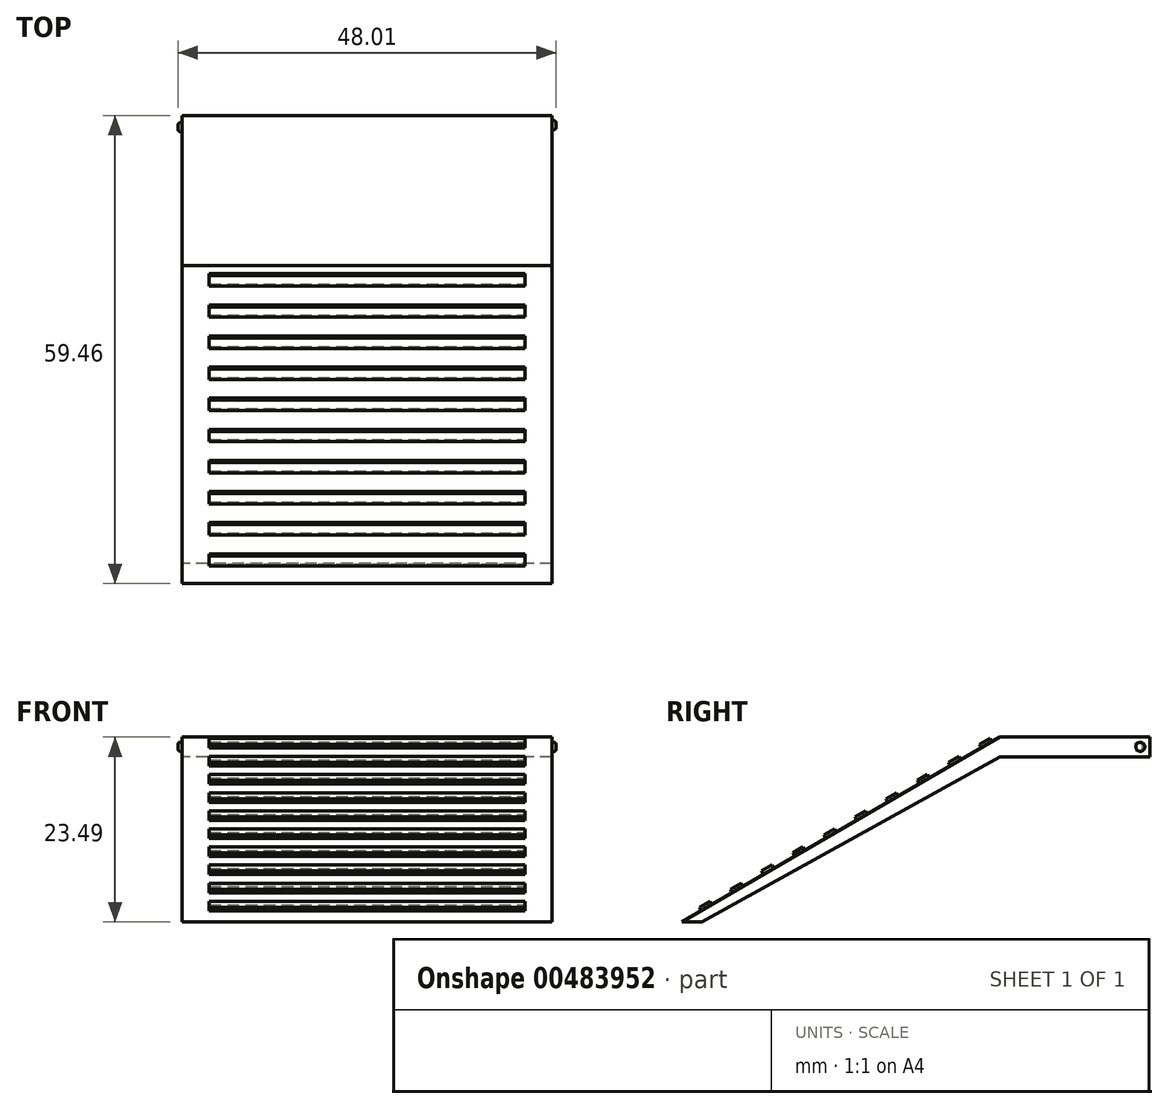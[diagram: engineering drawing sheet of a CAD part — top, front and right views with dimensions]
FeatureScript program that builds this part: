
annotation { "Feature Type Name" : "Feature", "Feature Type Description" : "" }
export const myFeature = defineFeature(function(context is Context, id is Id, definition is map)
    precondition{}
    {
        {
            var Q0;
            Q0=qCreatedBy(makeId("Right.planeOp"),FACE);
            var sketch = newSketch(context, id + "F0", { "sketchPlane" : qUnion([Q0])});
            skLineSegment(sketch, "E0.bottom", {"start": v(19.05, 2.54) * mm, "end": v(0, 2.54) * mm});
            skLineSegment(sketch, "E0.top", {"start": v(19.05, 0) * mm, "end": v(0, 0) * mm});
            skLineSegment(sketch, "E0.left", {"start": v(19.05, 2.54) * mm, "end": v(19.05, 0) * mm});
            skLineSegment(sketch, "E0.right", {"start": v(0, 2.54) * mm, "end": v(0, 0) * mm});
            skLineSegment(sketch, "E1", {"start": v(0, 2.54) * mm, "end": v(-40.41, -20.95) * mm});
            skLineSegment(sketch, "E2", {"start": v(-40.41, -20.95) * mm, "end": v(-37.87, -20.95) * mm});
            skLineSegment(sketch, "E3", {"start": v(-37.87, -20.95) * mm, "end": v(0, 0) * mm});
            skSolve(sketch);
        }
        {
            var Q0;
            Q0=makeQuery(id+"F0.imprint","IMPRINT",FACE,{"disambiguationData":[TD([[makeQuery(id+"F0.imprint","IMPRINT",EDGE,{"derivedFrom":sQuery(id+"F0.wireOp",EDGE,"E0.bottom")}),1.0]])]});
            var Q1;
            Q1=makeQuery(id+"F0.imprint","IMPRINT",FACE,{"disambiguationData":[TD([[makeQuery(id+"F0.imprint","IMPRINT",EDGE,{"derivedFrom":sQuery(id+"F0.wireOp",EDGE,"E0.right")}),-1.0]])]});
            extrude(context, id + "F1", {"entities" : qUnion([Q0, Q1]), "depth" : 47 * mm});
        }
        {
            var Q0;
            Q0=makeQuery(id+"F1.opExtrude","SWEPT_FACE",FACE,{"disambiguationData":[OSD([sQuery(id+"F0.wireOp",EDGE,"E1")])]});
            var sketch = newSketch(context, id + "F2", { "sketchPlane" : qUnion([Q0])});
            skLineSegment(sketch, "E4.bottom", {"start": v(3.45, -1.47) * mm, "end": v(43.54, -1.47) * mm});
            skLineSegment(sketch, "E4.top", {"start": v(3.45, 0.06) * mm, "end": v(43.54, 0.06) * mm});
            skLineSegment(sketch, "E4.left", {"start": v(3.45, -1.47) * mm, "end": v(3.45, 0.06) * mm});
            skLineSegment(sketch, "E4.right", {"start": v(43.54, -1.47) * mm, "end": v(43.54, 0.06) * mm});
            skPoint(sketch, "E4.middle", {"position": v(23.5, -0.7) * mm});
            skPoint(sketch, "E4.middle.positionSnap0", {"position": v(23.5, 1.28) * mm});
            skPoint(sketch, "E4.centerSnap0", {"position": v(23.5, 1.28) * mm});
            skLineSegment(sketch, "E5.0.1.0", {"start": v(3.45, -6.04) * mm, "end": v(3.45, -4.52) * mm});
            skLineSegment(sketch, "E5.0.1.1", {"start": v(3.45, -4.52) * mm, "end": v(43.54, -4.52) * mm});
            skLineSegment(sketch, "E5.0.1.2", {"start": v(43.54, -6.04) * mm, "end": v(43.54, -4.52) * mm});
            skLineSegment(sketch, "E5.0.1.3", {"start": v(3.45, -6.04) * mm, "end": v(43.54, -6.04) * mm});
            skLineSegment(sketch, "E5.0.2.0", {"start": v(3.45, -10.61) * mm, "end": v(3.45, -9.09) * mm});
            skLineSegment(sketch, "E5.0.2.1", {"start": v(3.45, -9.09) * mm, "end": v(43.54, -9.09) * mm});
            skLineSegment(sketch, "E5.0.2.2", {"start": v(43.54, -10.61) * mm, "end": v(43.54, -9.09) * mm});
            skLineSegment(sketch, "E5.0.2.3", {"start": v(3.45, -10.61) * mm, "end": v(43.54, -10.61) * mm});
            skLineSegment(sketch, "E5.0.3.0", {"start": v(3.45, -15.18) * mm, "end": v(3.45, -13.66) * mm});
            skLineSegment(sketch, "E5.0.3.1", {"start": v(3.45, -13.66) * mm, "end": v(43.54, -13.66) * mm});
            skLineSegment(sketch, "E5.0.3.2", {"start": v(43.54, -15.18) * mm, "end": v(43.54, -13.66) * mm});
            skLineSegment(sketch, "E5.0.3.3", {"start": v(3.45, -15.18) * mm, "end": v(43.54, -15.18) * mm});
            skLineSegment(sketch, "E5.0.4.0", {"start": v(3.45, -19.76) * mm, "end": v(3.45, -18.23) * mm});
            skLineSegment(sketch, "E5.0.4.1", {"start": v(3.45, -18.23) * mm, "end": v(43.54, -18.23) * mm});
            skLineSegment(sketch, "E5.0.4.2", {"start": v(43.54, -19.76) * mm, "end": v(43.54, -18.23) * mm});
            skLineSegment(sketch, "E5.0.4.3", {"start": v(3.45, -19.76) * mm, "end": v(43.54, -19.76) * mm});
            skLineSegment(sketch, "E5.0.5.0", {"start": v(3.45, -24.33) * mm, "end": v(3.45, -22.8) * mm});
            skLineSegment(sketch, "E5.0.5.1", {"start": v(3.45, -22.8) * mm, "end": v(43.54, -22.8) * mm});
            skLineSegment(sketch, "E5.0.5.2", {"start": v(43.54, -24.33) * mm, "end": v(43.54, -22.8) * mm});
            skLineSegment(sketch, "E5.0.5.3", {"start": v(3.45, -24.33) * mm, "end": v(43.54, -24.33) * mm});
            skLineSegment(sketch, "E5.0.6.0", {"start": v(3.45, -28.9) * mm, "end": v(3.45, -27.38) * mm});
            skLineSegment(sketch, "E5.0.6.1", {"start": v(3.45, -27.38) * mm, "end": v(43.54, -27.38) * mm});
            skLineSegment(sketch, "E5.0.6.2", {"start": v(43.54, -28.9) * mm, "end": v(43.54, -27.38) * mm});
            skLineSegment(sketch, "E5.0.6.3", {"start": v(3.45, -28.9) * mm, "end": v(43.54, -28.9) * mm});
            skLineSegment(sketch, "E5.0.7.0", {"start": v(3.45, -33.47) * mm, "end": v(3.45, -31.95) * mm});
            skLineSegment(sketch, "E5.0.7.1", {"start": v(3.45, -31.95) * mm, "end": v(43.54, -31.95) * mm});
            skLineSegment(sketch, "E5.0.7.2", {"start": v(43.54, -33.47) * mm, "end": v(43.54, -31.95) * mm});
            skLineSegment(sketch, "E5.0.7.3", {"start": v(3.45, -33.47) * mm, "end": v(43.54, -33.47) * mm});
            skLineSegment(sketch, "E5.0.8.0", {"start": v(3.45, -38.04) * mm, "end": v(3.45, -36.52) * mm});
            skLineSegment(sketch, "E5.0.8.1", {"start": v(3.45, -36.52) * mm, "end": v(43.54, -36.52) * mm});
            skLineSegment(sketch, "E5.0.8.2", {"start": v(43.54, -38.04) * mm, "end": v(43.54, -36.52) * mm});
            skLineSegment(sketch, "E5.0.8.3", {"start": v(3.45, -38.04) * mm, "end": v(43.54, -38.04) * mm});
            skLineSegment(sketch, "E5.0.9.0", {"start": v(3.45, -42.62) * mm, "end": v(3.45, -41.1) * mm});
            skLineSegment(sketch, "E5.0.9.1", {"start": v(3.45, -41.1) * mm, "end": v(43.54, -41.1) * mm});
            skLineSegment(sketch, "E5.0.9.2", {"start": v(43.54, -42.62) * mm, "end": v(43.54, -41.1) * mm});
            skLineSegment(sketch, "E5.0.9.3", {"start": v(3.45, -42.62) * mm, "end": v(43.54, -42.62) * mm});
            skLineSegment(sketch, "E5.direction1", {"start": v(3.45, -1.47) * mm, "end": v(28.85, -1.47) * mm, "construction": true});
            skLineSegment(sketch, "E5.direction2", {"start": v(3.45, -1.47) * mm, "end": v(3.45, -6.04) * mm, "construction": true});
            skSolve(sketch);
        }
        {
            var Q0;
            Q0=makeQuery(id+"F2.imprint","IMPRINT",FACE,{"disambiguationData":[TD([[makeQuery(id+"F2.imprint","IMPRINT",EDGE,{"derivedFrom":sQuery(id+"F2.wireOp",EDGE,"E4.bottom")}),1.0]])]});
            var Q1;
            Q1=makeQuery(id+"F2.imprint","IMPRINT",FACE,{"disambiguationData":[TD([[makeQuery(id+"F2.imprint","IMPRINT",EDGE,{"derivedFrom":sQuery(id+"F2.wireOp",EDGE,"E5.0.1.0")}),-1.0]])]});
            var Q2;
            Q2=makeQuery(id+"F2.imprint","IMPRINT",FACE,{"disambiguationData":[TD([[makeQuery(id+"F2.imprint","IMPRINT",EDGE,{"derivedFrom":sQuery(id+"F2.wireOp",EDGE,"E5.0.2.0")}),-1.0]])]});
            var Q3;
            Q3=makeQuery(id+"F2.imprint","IMPRINT",FACE,{"disambiguationData":[TD([[makeQuery(id+"F2.imprint","IMPRINT",EDGE,{"derivedFrom":sQuery(id+"F2.wireOp",EDGE,"E5.0.3.0")}),-1.0]])]});
            var Q4;
            Q4=makeQuery(id+"F2.imprint","IMPRINT",FACE,{"disambiguationData":[TD([[makeQuery(id+"F2.imprint","IMPRINT",EDGE,{"derivedFrom":sQuery(id+"F2.wireOp",EDGE,"E5.0.4.0")}),-1.0]])]});
            var Q5;
            Q5=makeQuery(id+"F2.imprint","IMPRINT",FACE,{"disambiguationData":[TD([[makeQuery(id+"F2.imprint","IMPRINT",EDGE,{"derivedFrom":sQuery(id+"F2.wireOp",EDGE,"E5.0.5.0")}),-1.0]])]});
            var Q6;
            Q6=makeQuery(id+"F2.imprint","IMPRINT",FACE,{"disambiguationData":[TD([[makeQuery(id+"F2.imprint","IMPRINT",EDGE,{"derivedFrom":sQuery(id+"F2.wireOp",EDGE,"E5.0.6.0")}),-1.0]])]});
            var Q7;
            Q7=makeQuery(id+"F2.imprint","IMPRINT",FACE,{"disambiguationData":[TD([[makeQuery(id+"F2.imprint","IMPRINT",EDGE,{"derivedFrom":sQuery(id+"F2.wireOp",EDGE,"E5.0.7.0")}),-1.0]])]});
            var Q8;
            Q8=makeQuery(id+"F2.imprint","IMPRINT",FACE,{"disambiguationData":[TD([[makeQuery(id+"F2.imprint","IMPRINT",EDGE,{"derivedFrom":sQuery(id+"F2.wireOp",EDGE,"E5.0.8.0")}),-1.0]])]});
            var Q9;
            Q9=makeQuery(id+"F2.imprint","IMPRINT",FACE,{"disambiguationData":[TD([[makeQuery(id+"F2.imprint","IMPRINT",EDGE,{"derivedFrom":sQuery(id+"F2.wireOp",EDGE,"E5.0.9.0")}),-1.0]])]});
            extrude(context, id + "F3", {"entities" : qUnion([Q0, Q1, Q2, Q3, Q4, Q5, Q6, Q7, Q8, Q9]), "operationType" : NewBodyOperationType.ADD, "depth" : 0.5 * mm});
        }
        {
            var Q0;
            Q0=makeQuery(id+"F1.opExtrude","CAP_FACE",FACE,{"disambiguationData":[OSD([sQuery(id+"F0.wireOp",EDGE,"E0.bottom"),sQuery(id+"F0.wireOp",EDGE,"E0.top"),sQuery(id+"F0.wireOp",EDGE,"E0.left"),sQuery(id+"F0.wireOp",EDGE,"E1"),sQuery(id+"F0.wireOp",EDGE,"E2"),sQuery(id+"F0.wireOp",EDGE,"E3")])],"isStart":true});
            var sketch = newSketch(context, id + "F4", { "sketchPlane" : qUnion([Q0])});
            skCircle(sketch, "E6", {"center": v(-17.56, 1.32) * mm, "radius": 0.57 * mm});
            skSolve(sketch);
        }
        {
            var Q0;
            Q0=makeQuery(id+"F4.imprint","IMPRINT",FACE,{"disambiguationData":[TD([[makeQuery(id+"F4.imprint","IMPRINT",EDGE,{"derivedFrom":sQuery(id+"F4.wireOp",EDGE,"E6")}),1.0]])]});
            extrude(context, id + "F5", {"entities" : qUnion([Q0]), "operationType" : NewBodyOperationType.ADD, "depth" : 0.5 * mm});
        }
        {
            var Q0;
            Q0=makeQuery(id+"F5.opExtrude","CAP_EDGE",EDGE,{"disambiguationData":[OSD([sQuery(id+"F4.wireOp",EDGE,"E6")])],"isStart":false});
            fillet(context, id + "F6", {"entities" : qUnion([Q0]), "radius" : 0.25 * mm, "tangentPropagation" : true, "allowEdgeOverflow" : false});
        }
        {
            var Q0;
            Q0=makeQuery(id+"F1.opExtrude","CAP_FACE",FACE,{"disambiguationData":[OSD([sQuery(id+"F0.wireOp",EDGE,"E0.bottom"),sQuery(id+"F0.wireOp",EDGE,"E0.top"),sQuery(id+"F0.wireOp",EDGE,"E0.left"),sQuery(id+"F0.wireOp",EDGE,"E1"),sQuery(id+"F0.wireOp",EDGE,"E2"),sQuery(id+"F0.wireOp",EDGE,"E3")])],"isStart":false});
            var sketch = newSketch(context, id + "F7", { "sketchPlane" : qUnion([Q0])});
            skCircle(sketch, "E7", {"center": v(17.81, 1.3) * mm, "radius": 0.57 * mm});
            skSolve(sketch);
        }
        {
            var Q0;
            Q0=makeQuery(id+"F7.imprint","IMPRINT",FACE,{"disambiguationData":[TD([[makeQuery(id+"F7.imprint","IMPRINT",EDGE,{"derivedFrom":sQuery(id+"F7.wireOp",EDGE,"E7")}),1.0]])]});
            extrude(context, id + "F8", {"entities" : qUnion([Q0]), "operationType" : NewBodyOperationType.ADD, "depth" : 0.5 * mm});
        }
        {
            var Q0;
            Q0=makeQuery(id+"F8.opExtrude","CAP_EDGE",EDGE,{"disambiguationData":[OSD([sQuery(id+"F7.wireOp",EDGE,"E7")])],"isStart":false});
            fillet(context, id + "F9", {"entities" : qUnion([Q0]), "radius" : 0.25 * mm, "tangentPropagation" : true, "allowEdgeOverflow" : false});
        }
    });
